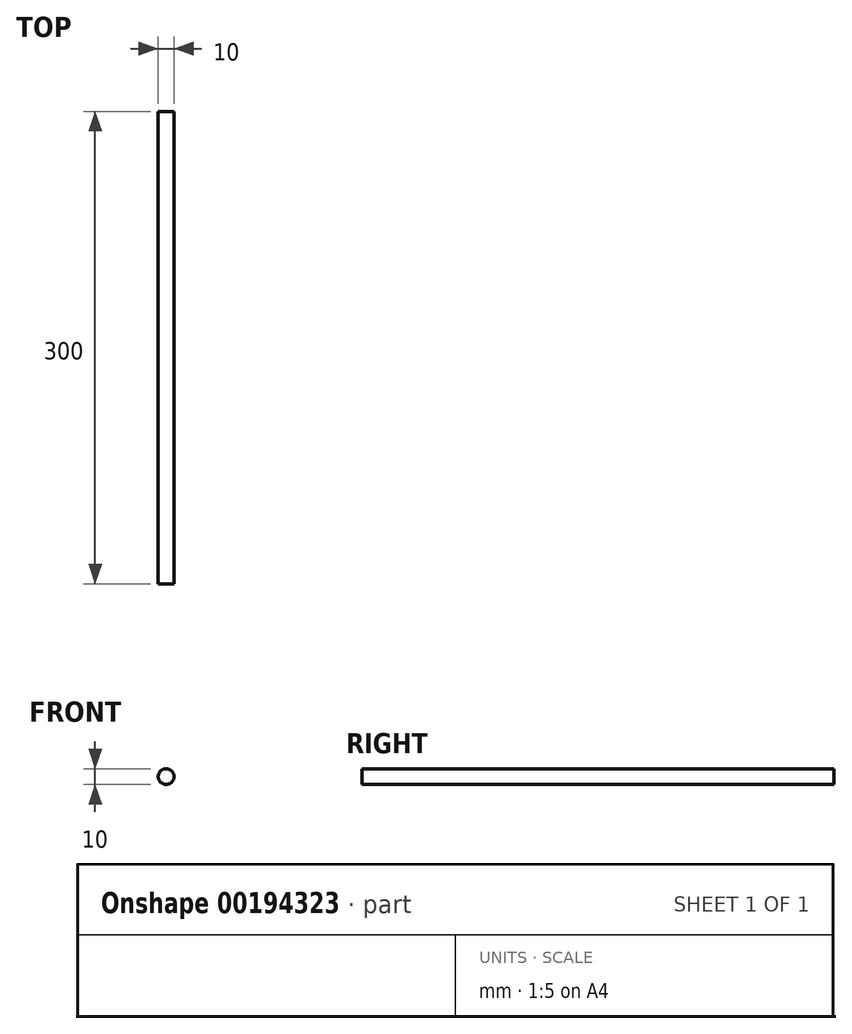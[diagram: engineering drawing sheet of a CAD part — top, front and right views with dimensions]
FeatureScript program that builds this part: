
annotation { "Feature Type Name" : "Feature", "Feature Type Description" : "" }
export const myFeature = defineFeature(function(context is Context, id is Id, definition is map)
    precondition{}
    {
        {
            var Q0;
            Q0=qCreatedBy(makeId("Front.planeOp"),FACE);
            var sketch = newSketch(context, id + "F0", { "sketchPlane" : qUnion([Q0])});
            skCircle(sketch, "E0", {"center": v(0, 0) * mm, "radius": 5 * mm});
            skSolve(sketch);
        }
        {
            var Q0;
            Q0=qSketchRegion(id+"F0",true);
            extrude(context, id + "F1", {"entities" : qUnion([Q0]), "depth" : 150 * mm, "hasSecondDirection" : true, "secondDirectionOppositeDirection" : true, "secondDirectionDepth" : 150 * mm});
        }
    });
